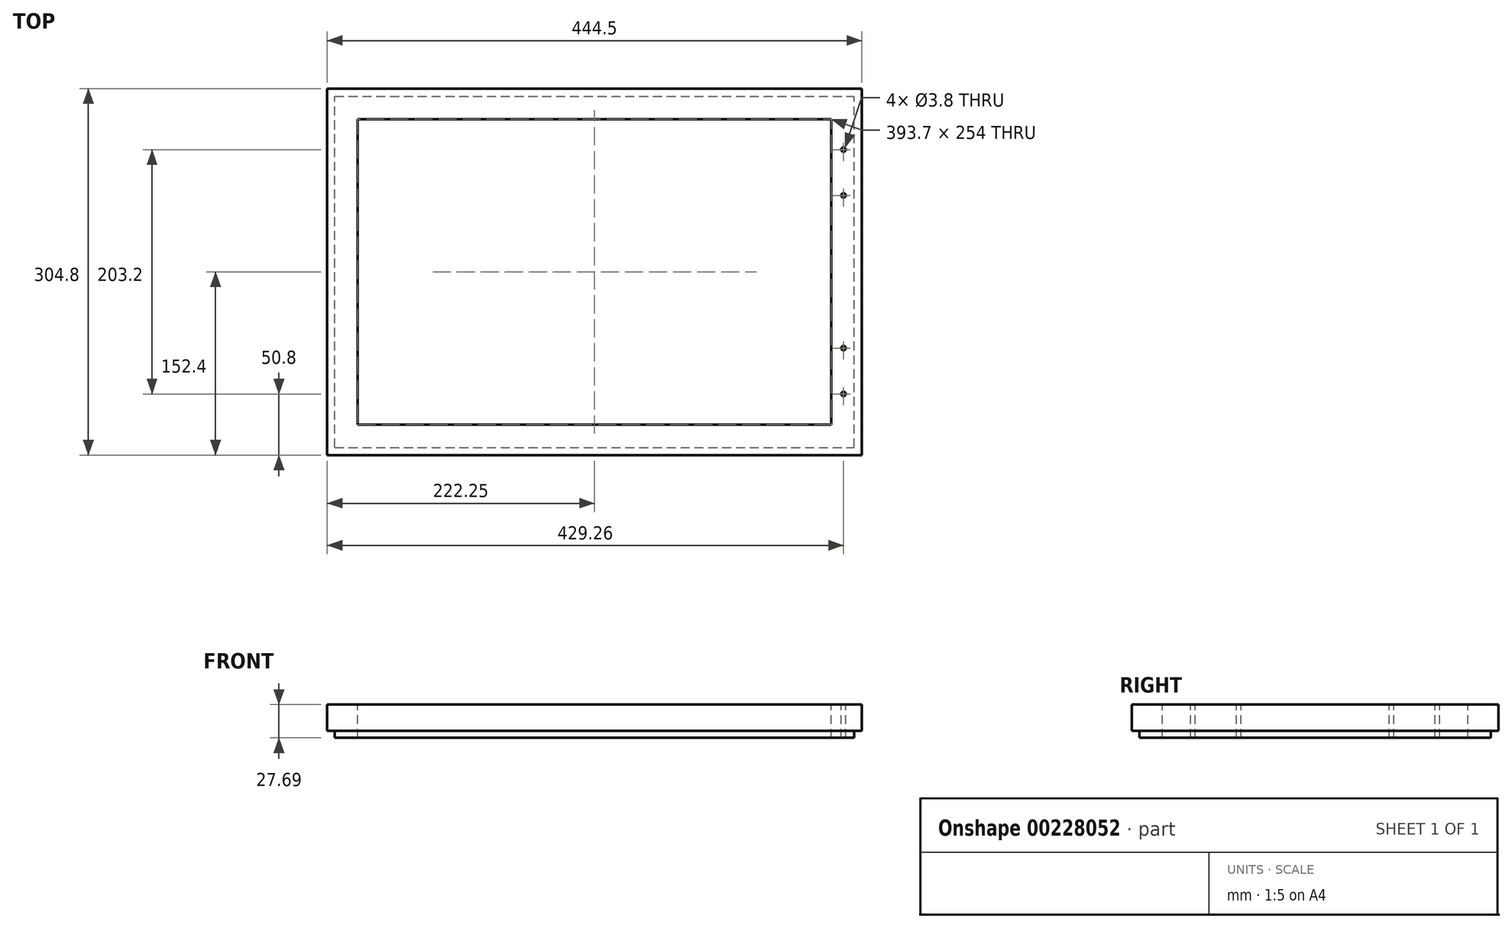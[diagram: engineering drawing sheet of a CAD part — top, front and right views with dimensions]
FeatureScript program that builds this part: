
annotation { "Feature Type Name" : "Feature", "Feature Type Description" : "" }
export const myFeature = defineFeature(function(context is Context, id is Id, definition is map)
    precondition{}
    {
        {
            var Q0;
            Q0=qCreatedBy(makeId("Top.planeOp"),FACE);
            var sketch = newSketch(context, id + "F0", { "sketchPlane" : qUnion([Q0])});
            skLineSegment(sketch, "E0.bottom", {"start": v(0, 0) * mm, "end": v(444.5, 0) * mm});
            skLineSegment(sketch, "E0.top", {"start": v(0, 304.8) * mm, "end": v(444.5, 304.8) * mm});
            skLineSegment(sketch, "E0.left", {"start": v(0, 0) * mm, "end": v(0, 304.8) * mm});
            skLineSegment(sketch, "E0.right", {"start": v(444.5, 0) * mm, "end": v(444.5, 304.8) * mm});
            skSolve(sketch);
        }
        {
            var Q0;
            Q0 = qSketchRegion(id + "F0", true);
            extrude(context, id + "F1", {"entities" : qUnion([Q0]), "depth" : 21.97 * mm});
        }
        {
            var Q0;
            Q0=makeQuery(id+"F1.opExtrude","CAP_FACE",FACE,{"disambiguationData":[OSD([sQuery(id+"F0.wireOp",EDGE,"E0.bottom"),sQuery(id+"F0.wireOp",EDGE,"E0.top"),sQuery(id+"F0.wireOp",EDGE,"E0.left"),sQuery(id+"F0.wireOp",EDGE,"E0.right")])],"isStart":true});
            var sketch = newSketch(context, id + "F2", { "sketchPlane" : qUnion([Q0])});
            skLineSegment(sketch, "E1.bottom", {"start": v(6.35, -6.35) * mm, "end": v(438.15, -6.35) * mm});
            skLineSegment(sketch, "E1.top", {"start": v(6.35, -298.45) * mm, "end": v(438.15, -298.45) * mm});
            skLineSegment(sketch, "E1.left", {"start": v(6.35, -6.35) * mm, "end": v(6.35, -298.45) * mm});
            skLineSegment(sketch, "E1.right", {"start": v(438.15, -6.35) * mm, "end": v(438.15, -298.45) * mm});
            skSolve(sketch);
        }
        {
            var Q0;
            Q0 = qSketchRegion(id + "F2", true);
            extrude(context, id + "F3", {"entities" : qUnion([Q0]), "operationType" : NewBodyOperationType.ADD, "depth" : 5.7 * mm});
        }
        {
            var Q0;
            Q0=makeQuery(id+"F1.opExtrude","CAP_FACE",FACE,{"disambiguationData":[OSD([sQuery(id+"F0.wireOp",EDGE,"E0.bottom"),sQuery(id+"F0.wireOp",EDGE,"E0.top"),sQuery(id+"F0.wireOp",EDGE,"E0.left"),sQuery(id+"F0.wireOp",EDGE,"E0.right")])],"isStart":false});
            var sketch = newSketch(context, id + "F4", { "sketchPlane" : qUnion([Q0])});
            skLineSegment(sketch, "E2.bottom", {"start": v(94.92, 87.47) * mm, "end": v(349.59, 87.47) * mm});
            skLineSegment(sketch, "E2.top", {"start": v(94.92, 220.47) * mm, "end": v(349.59, 220.47) * mm});
            skLineSegment(sketch, "E2.left", {"start": v(94.92, 87.47) * mm, "end": v(94.92, 220.47) * mm});
            skLineSegment(sketch, "E2.right", {"start": v(349.59, 87.47) * mm, "end": v(349.59, 220.47) * mm});
            skSolve(sketch);
        }
        {
            var Q0;
            Q0=makeQuery(id+"F4.imprint","IMPRINT",FACE,{"disambiguationData":[TD([[makeQuery(id+"F4.imprint","IMPRINT",EDGE,{"derivedFrom":sQuery(id+"F4.wireOp",EDGE,"E2.bottom")}),-1.0]])]});
            var sketch = newSketch(context, id + "F5", { "sketchPlane" : qUnion([Q0])});
            skLineSegment(sketch, "E3.bottom", {"start": v(25.4, 279.4) * mm, "end": v(419.1, 279.4) * mm});
            skLineSegment(sketch, "E3.top", {"start": v(25.4, 25.4) * mm, "end": v(419.1, 25.4) * mm});
            skLineSegment(sketch, "E3.left", {"start": v(25.4, 279.4) * mm, "end": v(25.4, 25.4) * mm});
            skLineSegment(sketch, "E3.right", {"start": v(419.1, 279.4) * mm, "end": v(419.1, 25.4) * mm});
            skSolve(sketch);
        }
        {
            var Q0;
            Q0 = qSketchRegion(id + "F5", true);
            extrude(context, id + "F6", {"entities" : qUnion([Q0]), "operationType" : NewBodyOperationType.REMOVE, "endBound" : BoundingType.THROUGH_ALL, "oppositeDirection" : true, "depth" : 25.4 * mm});
        }
        {
            var Q0;
            Q0=makeQuery(id+"F4.imprint","IMPRINT",FACE,{"disambiguationData":[TD([[makeQuery(id+"F4.imprint","IMPRINT",EDGE,{"derivedFrom":sQuery(id+"F4.wireOp",EDGE,"E2.bottom")}),-1.0]])]});
            var sketch = newSketch(context, id + "F7", { "sketchPlane" : qUnion([Q0])});
            skSolve(sketch);
        }
        {
            var Q0;
            Q0=makeQuery(id+"F4.imprint","IMPRINT",FACE,{"disambiguationData":[TD([[makeQuery(id+"F4.imprint","IMPRINT",EDGE,{"derivedFrom":sQuery(id+"F4.wireOp",EDGE,"E2.bottom")}),-1.0]])]});
            var sketch = newSketch(context, id + "F8", { "sketchPlane" : qUnion([Q0])});
            skPoint(sketch, "E4", {"position": v(429.26, 88.9) * mm});
            skPoint(sketch, "E5", {"position": v(429.26, 50.8) * mm});
            skPoint(sketch, "E6", {"position": v(429.26, 254) * mm});
            skPoint(sketch, "E7", {"position": v(429.26, 215.9) * mm});
            skSolve(sketch);
        }
        {
            var Q0;
            Q0=sQuery(id+"F8.wireOp",VERTEX,"E6");
            var Q1;
            Q1=sQuery(id+"F8.wireOp",VERTEX,"E7");
            var Q2;
            Q2=sQuery(id+"F8.wireOp",VERTEX,"E4");
            var Q3;
            Q3=sQuery(id+"F8.wireOp",VERTEX,"E5");
            var Q4;
            Q4=makeQuery(id+"F1.opExtrude","SWEPT_BODY",BODY,{"disambiguationData":[OSD([sQuery(id+"F0.wireOp",EDGE,"E0.bottom"),sQuery(id+"F0.wireOp",EDGE,"E0.top"),sQuery(id+"F0.wireOp",EDGE,"E0.left"),sQuery(id+"F0.wireOp",EDGE,"E0.right")])]});
            hole(context, id + "F9", {"style" : HoleStyle.SIMPLE, "endStyle" : HoleEndStyle.THROUGH, "standardTappedOrClearance" : lookupTablePath({ "standard" : "ANSI", "fit" : "Normal (ASME)", "size" : "#6", "type" : "Clearance" }), "standardBlindInLast" : lookupTablePath({ "fit" : "Free", "standard" : "ANSI", "size" : "#6", "type" : "Clearance" }), "holeDiameter" : 3.8 * mm, "locations" : qUnion([Q0, Q1, Q2, Q3]), "scope" : qUnion([Q4]), "isTappedThrough" : true});
        }
    });
